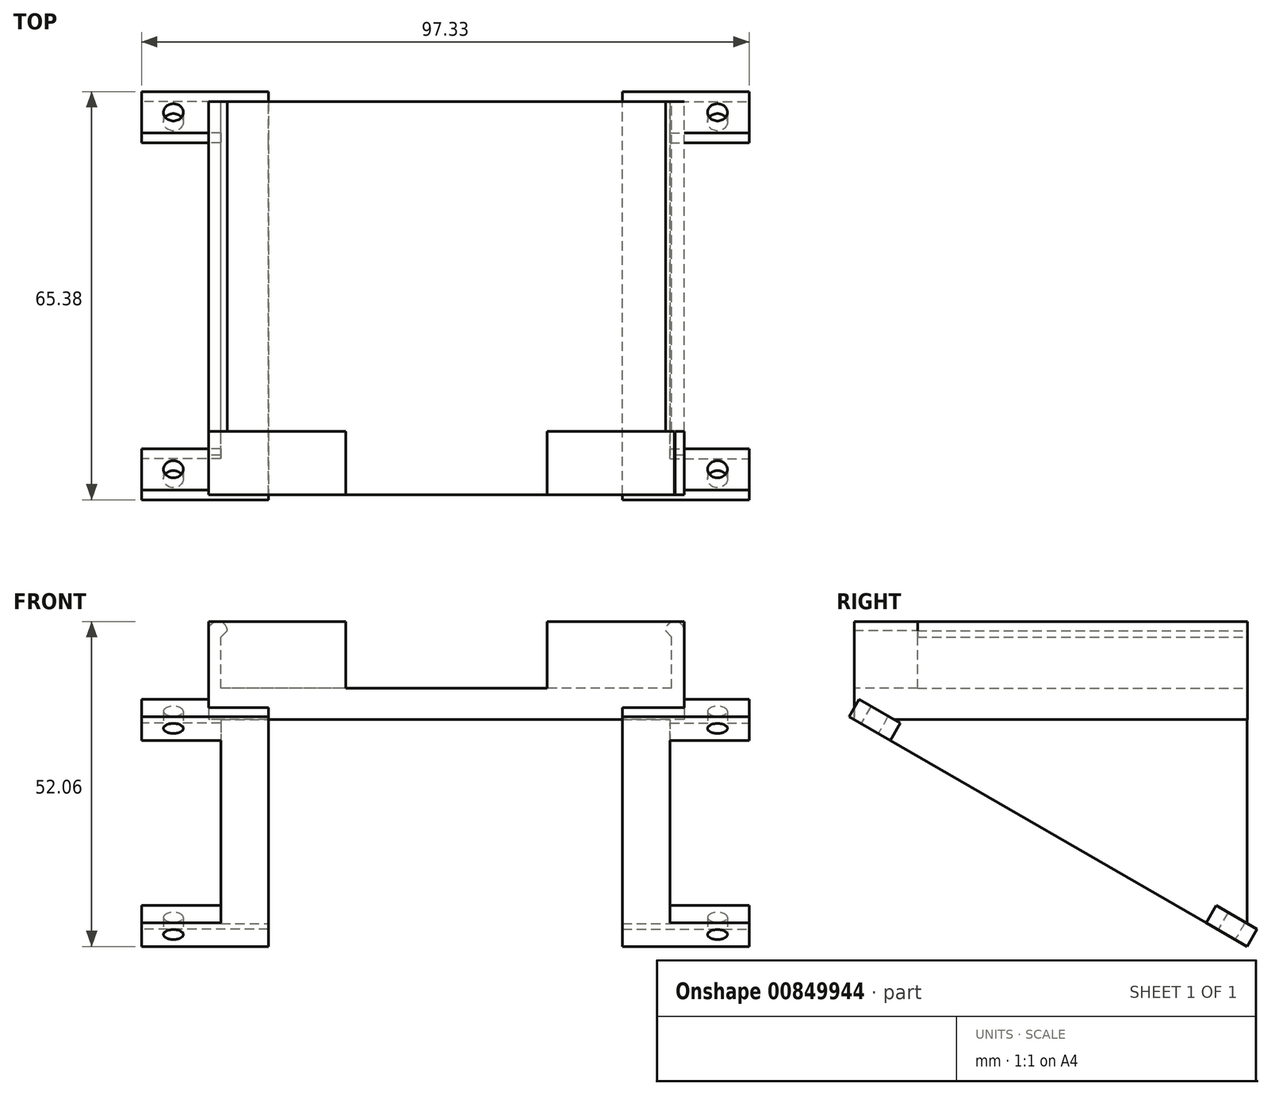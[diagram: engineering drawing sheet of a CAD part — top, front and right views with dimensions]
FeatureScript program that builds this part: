
annotation { "Feature Type Name" : "Feature", "Feature Type Description" : "" }
export const myFeature = defineFeature(function(context is Context, id is Id, definition is map)
    precondition{}
    {
        {
            var Q0;
            Q0=qCreatedBy(makeId("Right.planeOp"),FACE);
            var sketch = newSketch(context, id + "F0", { "sketchPlane" : qUnion([Q0])});
            skLineSegment(sketch, "E0.bottom", {"start": v(-31.5, -5.35) * mm, "end": v(-28.98, -5.35) * mm});
            skLineSegment(sketch, "E0.top", {"start": v(-31.5, -7.85) * mm, "end": v(-28.98, -7.85) * mm});
            skLineSegment(sketch, "E0.left", {"start": v(-31.5, -5.35) * mm, "end": v(-31.5, -7.85) * mm});
            skLineSegment(sketch, "E0.right", {"start": v(-28.98, -5.35) * mm, "end": v(-28.98, -7.85) * mm});
            skLineSegment(sketch, "E1", {"start": v(-31.5, -7.85) * mm, "end": v(31.48, -44.2) * mm});
            skLineSegment(sketch, "E2", {"start": v(31.48, -7.85) * mm, "end": v(31.48, -44.2) * mm});
            skLineSegment(sketch, "E3", {"start": v(31.48, -7.85) * mm, "end": v(-28.98, -7.85) * mm});
            skSolve(sketch);
        }
        {
            var Q0;
            Q0 = qSketchRegion(id + "F0", true);
            var Q1;
            Q1 = qConstructionFilter(qBodyType(qCreatedBy(id + "F0" ,EDGE), BodyType.WIRE), ConstructionObject.NO);
            extrude(context, id + "F1", {"entities" : qUnion([Q0]), "surfaceOperationType" : NewSurfaceOperationType.ADD, "surfaceEntities" : qUnion([Q1]), "depth" : -7.62 * mm, "offsetDistance" : 25.4 * mm});
        }
        {
            var Q0;
            Q0=makeQuery(id+"F1.opExtrude","SWEPT_BODY",BODY,{"disambiguationData":[OSD([sQuery(id+"F0.wireOp",EDGE,"E0.bottom"),sQuery(id+"F0.wireOp",EDGE,"E0.left"),sQuery(id+"F0.wireOp",EDGE,"E0.right"),sQuery(id+"F0.wireOp",EDGE,"E1"),sQuery(id+"F0.wireOp",EDGE,"E2"),sQuery(id+"F0.wireOp",EDGE,"E3")])]});
            transform(context, id + "F2", {"entities" : qUnion([Q0]), "transformType" : TransformType.TRANSLATION_3D, "dx" : 35.81 * mm, "dy" : 0 * mm, "dz" : 0 * mm, "makeCopy" : false});
        }
        {
            var Q0;
            Q0=makeQuery(id+"F1.opExtrude","SWEPT_BODY",BODY,{"disambiguationData":[OSD([sQuery(id+"F0.wireOp",EDGE,"E0.bottom"),sQuery(id+"F0.wireOp",EDGE,"E0.left"),sQuery(id+"F0.wireOp",EDGE,"E0.right"),sQuery(id+"F0.wireOp",EDGE,"E1"),sQuery(id+"F0.wireOp",EDGE,"E2"),sQuery(id+"F0.wireOp",EDGE,"E3")])]});
            transform(context, id + "F3", {"entities" : qUnion([Q0]), "transformType" : TransformType.TRANSLATION_3D, "dx" : -64.31 * mm, "dy" : 0 * mm, "dz" : 0 * mm, "makeCopy" : true});
        }
        {
            var Q0;
            Q0=qCreatedBy(makeId("Front.planeOp"),FACE);
            var sketch = newSketch(context, id + "F4", { "sketchPlane" : qUnion([Q0])});
            skPoint(sketch, "E4.0", {"position": v(31.68, -2.85) * mm});
            skPoint(sketch, "E4.1", {"position": v(21.14, -7.85) * mm});
            skLineSegment(sketch, "E5.bottom", {"start": v(38.1, -2.85) * mm, "end": v(-38.1, -2.85) * mm});
            skLineSegment(sketch, "E5.top", {"start": v(38.1, -7.84) * mm, "end": v(-38.1, -7.84) * mm});
            skLineSegment(sketch, "E5.left", {"start": v(38.1, -2.85) * mm, "end": v(38.1, -7.84) * mm});
            skLineSegment(sketch, "E5.right", {"start": v(-38.1, -2.85) * mm, "end": v(-38.1, -7.84) * mm});
            skLineSegment(sketch, "E6.bottom", {"start": v(38.1, -2.85) * mm, "end": v(36.1, -2.85) * mm});
            skLineSegment(sketch, "E6.top", {"start": v(38.1, 5.35) * mm, "end": v(36.1, 5.35) * mm});
            skLineSegment(sketch, "E6.left", {"start": v(38.1, -2.85) * mm, "end": v(38.1, 5.35) * mm});
            skLineSegment(sketch, "E6.right", {"start": v(36.1, -2.85) * mm, "end": v(36.1, 5.35) * mm});
            skLineSegment(sketch, "E7.bottom", {"start": v(-38.1, -2.85) * mm, "end": v(-36.1, -2.85) * mm});
            skLineSegment(sketch, "E7.top", {"start": v(-38.1, 5.35) * mm, "end": v(-36.1, 5.35) * mm});
            skLineSegment(sketch, "E7.left", {"start": v(-38.1, -2.85) * mm, "end": v(-38.1, 5.35) * mm});
            skLineSegment(sketch, "E7.right", {"start": v(-36.1, -2.85) * mm, "end": v(-36.1, 5.35) * mm});
            skLineSegment(sketch, "E8", {"start": v(36.1, 5.35) * mm, "end": v(35.1, 6.35) * mm});
            skArc(sketch, "E9", {"start": v(36.62, 7.85) * mm, "mid": v(35.55, 7.42) * mm, "end": v(35.1, 6.35) * mm});
            skArc(sketch, "E10", {"start": v(38.1, 6.35) * mm, "mid": v(37.67, 7.4) * mm, "end": v(36.62, 7.85) * mm});
            skLineSegment(sketch, "E11", {"start": v(38.1, 6.35) * mm, "end": v(38.1, 5.35) * mm});
            skArc(sketch, "E12", {"start": v(-35.1, 6.35) * mm, "mid": v(-36.6, 7.85) * mm, "end": v(-38.1, 6.35) * mm});
            skLineSegment(sketch, "E13", {"start": v(-35.1, 6.35) * mm, "end": v(-36.1, 5.35) * mm});
            skLineSegment(sketch, "E14", {"start": v(-38.1, 6.35) * mm, "end": v(-38.1, 5.35) * mm});
            skSolve(sketch);
        }
        {
            var Q0;
            Q0 = qSketchRegion(id + "F4", true);
            extrude(context, id + "F5", {"entities" : qUnion([Q0]), "depth" : 31.5 * mm, "offsetDistance" : 25.4 * mm, "hasSecondDirection" : true, "secondDirectionOppositeDirection" : true, "secondDirectionDepth" : 31.5 * mm});
        }
        {
            var Q0;
            Q0=makeQuery(id+"F5.opExtrude","CAP_FACE",FACE,{"disambiguationData":[OSD([sQuery(id+"F4.wireOp",EDGE,"E5.bottom"),sQuery(id+"F4.wireOp",EDGE,"E5.top"),sQuery(id+"F4.wireOp",EDGE,"E5.left"),sQuery(id+"F4.wireOp",EDGE,"E5.right"),sQuery(id+"F4.wireOp",EDGE,"E6.left"),sQuery(id+"F4.wireOp",EDGE,"E6.right"),sQuery(id+"F4.wireOp",EDGE,"E7.top"),sQuery(id+"F4.wireOp",EDGE,"E7.left"),sQuery(id+"F4.wireOp",EDGE,"E7.right"),sQuery(id+"F4.wireOp",EDGE,"E8"),sQuery(id+"F4.wireOp",EDGE,"E9"),sQuery(id+"F4.wireOp",EDGE,"E10"),sQuery(id+"F4.wireOp",EDGE,"E11")])],"isStart":false});
            var sketch = newSketch(context, id + "F6", { "sketchPlane" : qUnion([Q0])});
            skLineSegment(sketch, "E15.bottom", {"start": v(-38.1, -7.84) * mm, "end": v(-16.13, -7.84) * mm});
            skLineSegment(sketch, "E15.top", {"start": v(-38.1, 7.85) * mm, "end": v(-16.13, 7.85) * mm});
            skLineSegment(sketch, "E15.left", {"start": v(-38.1, -7.84) * mm, "end": v(-38.1, 7.85) * mm});
            skLineSegment(sketch, "E15.right", {"start": v(-16.13, -7.84) * mm, "end": v(-16.13, 7.85) * mm});
            skLineSegment(sketch, "E16.bottom", {"start": v(-16.13, -7.84) * mm, "end": v(16.16, -7.84) * mm});
            skLineSegment(sketch, "E16.top", {"start": v(-16.13, -2.85) * mm, "end": v(16.16, -2.85) * mm});
            skLineSegment(sketch, "E16.left", {"start": v(-16.13, -7.84) * mm, "end": v(-16.13, -2.85) * mm});
            skLineSegment(sketch, "E16.right", {"start": v(16.16, -7.84) * mm, "end": v(16.16, -2.85) * mm});
            skLineSegment(sketch, "E17.bottom", {"start": v(16.16, -7.84) * mm, "end": v(38.1, -7.84) * mm});
            skLineSegment(sketch, "E17.top", {"start": v(16.16, 7.85) * mm, "end": v(38.1, 7.85) * mm});
            skLineSegment(sketch, "E17.left", {"start": v(16.16, -7.84) * mm, "end": v(16.16, 7.85) * mm});
            skLineSegment(sketch, "E17.right", {"start": v(38.1, -7.84) * mm, "end": v(38.1, 7.85) * mm});
            skSolve(sketch);
        }
        {
            var Q0;
            Q0 = qSketchRegion(id + "F6", true);
            extrude(context, id + "F7", {"entities" : qUnion([Q0]), "oppositeDirection" : true, "depth" : 10.16 * mm, "offsetDistance" : 25.4 * mm});
        }
        {
            var Q0;
            Q0=makeQuery(id+"F1.opExtrude","SWEPT_FACE",FACE,{"disambiguationData":[OSD([sQuery(id+"F0.wireOp",EDGE,"E1")])]});
            var sketch = newSketch(context, id + "F8", { "sketchPlane" : qUnion([Q0])});
            skLineSegment(sketch, "E18.bottom", {"start": v(28.2, -49.36) * mm, "end": v(48.51, -49.36) * mm});
            skLineSegment(sketch, "E18.top", {"start": v(28.2, -41.74) * mm, "end": v(48.51, -41.74) * mm});
            skLineSegment(sketch, "E18.left", {"start": v(28.2, -49.36) * mm, "end": v(28.2, -41.74) * mm});
            skLineSegment(sketch, "E18.right", {"start": v(48.51, -49.36) * mm, "end": v(48.51, -41.74) * mm});
            skCircle(sketch, "E19", {"center": v(43.43, -45.55) * mm, "radius": 1.59 * mm});
            skLineSegment(sketch, "E20.bottom", {"start": v(-28.5, -49.36) * mm, "end": v(-48.82, -49.36) * mm});
            skLineSegment(sketch, "E20.top", {"start": v(-28.5, -41.74) * mm, "end": v(-48.82, -41.74) * mm});
            skLineSegment(sketch, "E20.left", {"start": v(-28.5, -49.36) * mm, "end": v(-28.5, -41.74) * mm});
            skLineSegment(sketch, "E20.right", {"start": v(-48.82, -49.36) * mm, "end": v(-48.82, -41.74) * mm});
            skCircle(sketch, "E21", {"center": v(-43.74, -45.55) * mm, "radius": 1.59 * mm});
            skLineSegment(sketch, "E22.0.1.0", {"start": v(-28.5, 16.68) * mm, "end": v(-28.5, 24.3) * mm});
            skLineSegment(sketch, "E22.0.1.1", {"start": v(28.2, 16.68) * mm, "end": v(28.2, 24.3) * mm});
            skLineSegment(sketch, "E22.0.1.2", {"start": v(28.2, 16.68) * mm, "end": v(48.51, 16.68) * mm});
            skLineSegment(sketch, "E22.0.1.3", {"start": v(-48.82, 16.68) * mm, "end": v(-48.82, 24.3) * mm});
            skLineSegment(sketch, "E22.0.1.4", {"start": v(-28.5, 24.3) * mm, "end": v(-48.82, 24.3) * mm});
            skLineSegment(sketch, "E22.0.1.5", {"start": v(28.2, 24.3) * mm, "end": v(48.51, 24.3) * mm});
            skLineSegment(sketch, "E22.0.1.6", {"start": v(48.51, 16.68) * mm, "end": v(48.51, 24.3) * mm});
            skCircle(sketch, "E22.0.1.7", {"center": v(43.43, 20.49) * mm, "radius": 1.59 * mm});
            skLineSegment(sketch, "E22.0.1.8", {"start": v(-28.5, 16.68) * mm, "end": v(-48.82, 16.68) * mm});
            skCircle(sketch, "E22.0.1.9", {"center": v(-43.74, 20.49) * mm, "radius": 1.59 * mm});
            skLineSegment(sketch, "E22.direction1", {"start": v(-48.82, -49.36) * mm, "end": v(-23.42, -49.36) * mm, "construction": true});
            skLineSegment(sketch, "E22.direction2", {"start": v(-48.82, -49.36) * mm, "end": v(-48.82, 16.68) * mm, "construction": true});
            skSolve(sketch);
        }
        {
            var Q0;
            Q0 = qSketchRegion(id + "F8", true);
            extrude(context, id + "F9", {"entities" : qUnion([Q0]), "operationType" : NewBodyOperationType.ADD, "oppositeDirection" : true, "depth" : 3.17 * mm, "offsetDistance" : 25.4 * mm});
        }
    });
